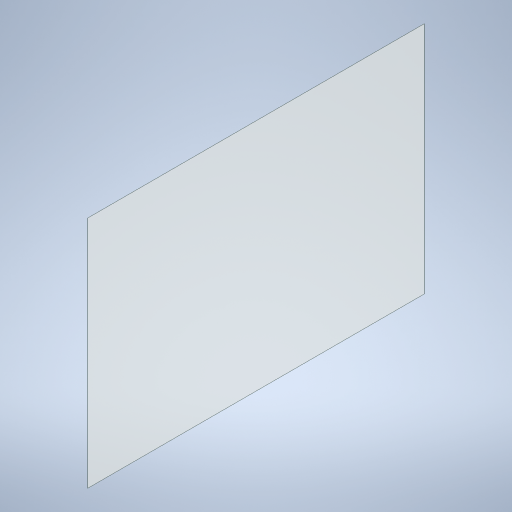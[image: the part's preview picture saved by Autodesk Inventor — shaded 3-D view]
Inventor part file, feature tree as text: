
AUTODESK INVENTOR PART (.ipt)
format: ipt  version: 2024 (Build 280153000, 153)  size: 215,040 bytes
history: native  units: in
note: dims shown in document units (in); Inventor stores cm internally (conversion verified against a paired STEP export)
features: extrude x1, sketch x1
ambient origin geometry x8: Origin, YZ Plane, XZ Plane, XY Plane, X Axis, Y Axis, Z Axis, Center Point
bodies: Solid1 (feature_tree)
feature tree (2):
  extrude  "Extrusion1"  Depth=208.632in
  sketch  "Sketch1"  dims[d2=300.0in d3=208.632in d4=0.125in d5=0.0in]
